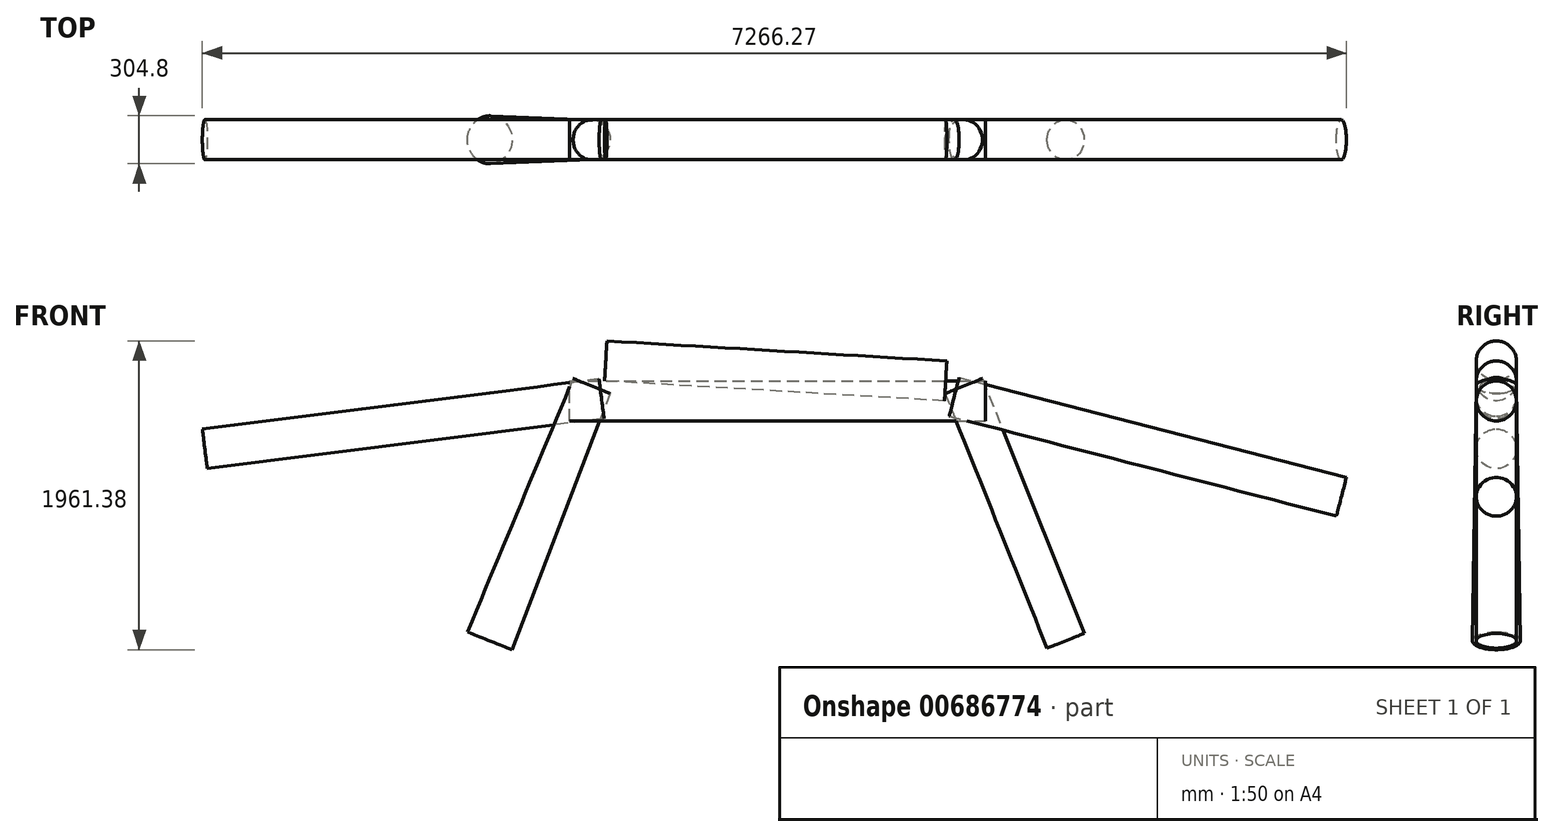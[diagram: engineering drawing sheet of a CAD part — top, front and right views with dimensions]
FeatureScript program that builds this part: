
annotation { "Feature Type Name" : "Feature", "Feature Type Description" : "" }
export const myFeature = defineFeature(function(context is Context, id is Id, definition is map)
    precondition{}
    {
        {
            var Q0;
            Q0=qCreatedBy(makeId("Front.planeOp"),FACE);
            var sketch = newSketch(context, id + "F0", { "sketchPlane" : qUnion([Q0])});
            skLineSegment(sketch, "E0", {"start": v(-1320.8, 0) * mm, "end": v(-1219.2, 0) * mm, "construction": true});
            skLineSegment(sketch, "E1", {"start": v(-1219.2, 0) * mm, "end": v(1219.2, 0) * mm, "construction": true});
            skLineSegment(sketch, "E2", {"start": v(1219.2, 0) * mm, "end": v(1320.8, 0) * mm, "construction": true});
            skLineSegment(sketch, "E3", {"start": v(-1181.47, 94.33) * mm, "end": v(-1219.2, 0) * mm, "construction": true});
            skLineSegment(sketch, "E4", {"start": v(-1219.2, 0) * mm, "end": v(-1828.8, -1524) * mm, "construction": true});
            skLineSegment(sketch, "E5", {"start": v(1181.47, 94.33) * mm, "end": v(1219.2, 0) * mm, "construction": true});
            skLineSegment(sketch, "E6", {"start": v(1219.2, 0) * mm, "end": v(1828.8, -1524) * mm, "construction": true});
            skLineSegment(sketch, "E7", {"start": v(1120.83, 25.4) * mm, "end": v(1219.2, 0) * mm, "construction": true});
            skLineSegment(sketch, "E8", {"start": v(1219.2, 0) * mm, "end": v(3580.17, -609.6) * mm, "construction": true});
            skLineSegment(sketch, "E9", {"start": v(-1118.4, 12.7) * mm, "end": v(-1219.2, 0) * mm, "construction": true});
            skLineSegment(sketch, "E10", {"start": v(-1219.2, 0) * mm, "end": v(-3638.47, -304.8) * mm, "construction": true});
            skLineSegment(sketch, "E11", {"start": v(1066.8, 127) * mm, "end": v(-1092.2, 254) * mm, "construction": true});
            skSolve(sketch);
        }
        {
            var Q0;
            Q0=sQuery(id+"F0.wireOp",EDGE,"E10");
            var Q1;
            Q1=sQuery(id+"F0.wireOp",VERTEX,"E10.end");
            cPlane(context, id + "F1", {"entities" : qUnion([Q0, Q1]), "cplaneType" : CPlaneType.LINE_POINT, "offset" : 25.4 * mm, "width" : 152.4 * mm, "height" : 152.4 * mm});
        }
        {
            var Q0;
            Q0=sQuery(id+"F0.wireOp",VERTEX,"E9.start");
            var Q1;
            Q1=sQuery(id+"F0.wireOp",EDGE,"E9");
            cPlane(context, id + "F2", {"entities" : qUnion([Q0, Q1]), "cplaneType" : CPlaneType.LINE_POINT, "offset" : 25.4 * mm, "width" : 152.4 * mm, "height" : 152.4 * mm});
        }
        {
            var Q0;
            Q0=qCreatedBy(id+"F1.planeOp",FACE);
            var sketch = newSketch(context, id + "F3", { "sketchPlane" : qUnion([Q0])});
            skCircle(sketch, "E12", {"center": v(0, 152.4) * mm, "radius": 127 * mm});
            skSolve(sketch);
        }
        {
            var Q0;
            Q0=qCreatedBy(id+"F2.planeOp",FACE);
            var sketch = newSketch(context, id + "F4", { "sketchPlane" : qUnion([Q0])});
            skCircle(sketch, "E13", {"center": v(0, 152.4) * mm, "radius": 127 * mm});
            skSolve(sketch);
        }
        {
            var Q0;
            Q0=makeQuery(id+"F3.imprint","IMPRINT",FACE,{"disambiguationData":[TD([[makeQuery(id+"F3.imprint","IMPRINT",EDGE,{"derivedFrom":sQuery(id+"F3.wireOp",EDGE,"E12")}),1.0]])]});
            var Q1;
            Q1=makeQuery(id+"F4.imprint","IMPRINT",FACE,{"disambiguationData":[TD([[makeQuery(id+"F4.imprint","IMPRINT",EDGE,{"derivedFrom":sQuery(id+"F4.wireOp",EDGE,"E13")}),1.0]])]});
            loft(context, id + "F5", {"sheetProfilesArray" : [{ "sheetProfileEntities" : qUnion([Q0]) }, { "sheetProfileEntities" : qUnion([Q1]) }]});
        }
        {
            var Q0;
            Q0=sQuery(id+"F0.wireOp",EDGE,"E4");
            var Q1;
            Q1=sQuery(id+"F0.wireOp",VERTEX,"E4.end");
            cPlane(context, id + "F6", {"entities" : qUnion([Q0, Q1]), "cplaneType" : CPlaneType.LINE_POINT, "offset" : 25.4 * mm, "width" : 152.4 * mm, "height" : 152.4 * mm});
        }
        {
            var Q0;
            Q0=sQuery(id+"F0.wireOp",VERTEX,"E3.start");
            var Q1;
            Q1=sQuery(id+"F0.wireOp",EDGE,"E3");
            cPlane(context, id + "F7", {"entities" : qUnion([Q0, Q1]), "cplaneType" : CPlaneType.LINE_POINT, "offset" : 25.4 * mm, "width" : 152.4 * mm, "height" : 152.4 * mm});
        }
        {
            var Q0;
            Q0=qCreatedBy(id+"F6.planeOp",FACE);
            var sketch = newSketch(context, id + "F8", { "sketchPlane" : qUnion([Q0])});
            skCircle(sketch, "E14", {"center": v(-1132, 0) * mm, "radius": 152.4 * mm});
            skSolve(sketch);
        }
        {
            var Q0;
            Q0=qCreatedBy(id+"F7.planeOp",FACE);
            var sketch = newSketch(context, id + "F9", { "sketchPlane" : qUnion([Q0])});
            skCircle(sketch, "E15", {"center": v(-1132, 0) * mm, "radius": 127 * mm});
            skSolve(sketch);
        }
        {
            var Q0;
            Q0=makeQuery(id+"F8.imprint","IMPRINT",FACE,{"disambiguationData":[TD([[makeQuery(id+"F8.imprint","IMPRINT",EDGE,{"derivedFrom":sQuery(id+"F8.wireOp",EDGE,"E14")}),1.0]])]});
            var Q1;
            Q1=makeQuery(id+"F9.imprint","IMPRINT",FACE,{"disambiguationData":[TD([[makeQuery(id+"F9.imprint","IMPRINT",EDGE,{"derivedFrom":sQuery(id+"F9.wireOp",EDGE,"E15")}),1.0]])]});
            loft(context, id + "F10", {"sheetProfilesArray" : [{ "sheetProfileEntities" : qUnion([Q0]) }, { "sheetProfileEntities" : qUnion([Q1]) }]});
        }
        {
            var Q0;
            Q0=sQuery(id+"F0.wireOp",EDGE,"E0");
            var Q1;
            Q1=sQuery(id+"F0.wireOp",VERTEX,"E0.start");
            cPlane(context, id + "F11", {"entities" : qUnion([Q0, Q1]), "cplaneType" : CPlaneType.LINE_POINT, "offset" : 25.4 * mm, "width" : 152.4 * mm, "height" : 152.4 * mm});
        }
        {
            var Q0;
            Q0=sQuery(id+"F0.wireOp",EDGE,"E2");
            var Q1;
            Q1=sQuery(id+"F0.wireOp",VERTEX,"E2.end");
            cPlane(context, id + "F12", {"entities" : qUnion([Q0, Q1]), "cplaneType" : CPlaneType.LINE_POINT, "offset" : 25.4 * mm, "width" : 152.4 * mm, "height" : 152.4 * mm});
        }
        {
            var Q0;
            Q0=qCreatedBy(id+"F12.planeOp",FACE);
            var sketch = newSketch(context, id + "F13", { "sketchPlane" : qUnion([Q0])});
            skCircle(sketch, "E16", {"center": v(0, 0) * mm, "radius": 127 * mm});
            skSolve(sketch);
        }
        {
            var Q0;
            Q0=qCreatedBy(id+"F11.planeOp",FACE);
            var sketch = newSketch(context, id + "F14", { "sketchPlane" : qUnion([Q0])});
            skCircle(sketch, "E17", {"center": v(0, 0) * mm, "radius": 127 * mm});
            skSolve(sketch);
        }
        {
            var Q0;
            Q0=makeQuery(id+"F14.imprint","IMPRINT",FACE,{"disambiguationData":[TD([[makeQuery(id+"F14.imprint","IMPRINT",EDGE,{"derivedFrom":sQuery(id+"F14.wireOp",EDGE,"E17")}),1.0]])]});
            var Q1;
            Q1=makeQuery(id+"F13.imprint","IMPRINT",FACE,{"disambiguationData":[TD([[makeQuery(id+"F13.imprint","IMPRINT",EDGE,{"derivedFrom":sQuery(id+"F13.wireOp",EDGE,"E16")}),1.0]])]});
            loft(context, id + "F15", {"sheetProfilesArray" : [{ "sheetProfileEntities" : qUnion([Q0]) }, { "sheetProfileEntities" : qUnion([Q1]) }]});
        }
        {
            var Q0;
            Q0=sQuery(id+"F0.wireOp",VERTEX,"E8.end");
            var Q1;
            Q1=sQuery(id+"F0.wireOp",EDGE,"E8");
            cPlane(context, id + "F16", {"entities" : qUnion([Q0, Q1]), "cplaneType" : CPlaneType.LINE_POINT, "offset" : 25.4 * mm, "width" : 152.4 * mm, "height" : 152.4 * mm});
        }
        {
            var Q0;
            Q0=sQuery(id+"F0.wireOp",EDGE,"E7");
            var Q1;
            Q1=sQuery(id+"F0.wireOp",VERTEX,"E7.start");
            cPlane(context, id + "F17", {"entities" : qUnion([Q0, Q1]), "cplaneType" : CPlaneType.LINE_POINT, "offset" : 25.4 * mm, "width" : 152.4 * mm, "height" : 152.4 * mm});
        }
        {
            var Q0;
            Q0=qCreatedBy(id+"F16.planeOp",FACE);
            var sketch = newSketch(context, id + "F18", { "sketchPlane" : qUnion([Q0])});
            skCircle(sketch, "E18", {"center": v(0, 304.8) * mm, "radius": 127 * mm});
            skSolve(sketch);
        }
        {
            var Q0;
            Q0=qCreatedBy(id+"F17.planeOp",FACE);
            var sketch = newSketch(context, id + "F19", { "sketchPlane" : qUnion([Q0])});
            skCircle(sketch, "E19", {"center": v(0, 304.8) * mm, "radius": 127 * mm});
            skSolve(sketch);
        }
        {
            var Q0;
            Q0=makeQuery(id+"F18.imprint","IMPRINT",FACE,{"disambiguationData":[TD([[makeQuery(id+"F18.imprint","IMPRINT",EDGE,{"derivedFrom":sQuery(id+"F18.wireOp",EDGE,"E18")}),1.0]])]});
            var Q1;
            Q1=makeQuery(id+"F19.imprint","IMPRINT",FACE,{"disambiguationData":[TD([[makeQuery(id+"F19.imprint","IMPRINT",EDGE,{"derivedFrom":sQuery(id+"F19.wireOp",EDGE,"E19")}),1.0]])]});
            loft(context, id + "F20", {"sheetProfilesArray" : [{ "sheetProfileEntities" : qUnion([Q0]) }, { "sheetProfileEntities" : qUnion([Q1]) }]});
        }
        {
            var Q0;
            Q0=sQuery(id+"F0.wireOp",EDGE,"E6");
            var Q1;
            Q1=sQuery(id+"F0.wireOp",VERTEX,"E6.end");
            cPlane(context, id + "F21", {"entities" : qUnion([Q0, Q1]), "cplaneType" : CPlaneType.LINE_POINT, "offset" : 25.4 * mm, "width" : 152.4 * mm, "height" : 152.4 * mm});
        }
        {
            var Q0;
            Q0=sQuery(id+"F0.wireOp",EDGE,"E5");
            var Q1;
            Q1=sQuery(id+"F0.wireOp",VERTEX,"E5.start");
            cPlane(context, id + "F22", {"entities" : qUnion([Q0, Q1]), "cplaneType" : CPlaneType.LINE_POINT, "offset" : 25.4 * mm, "width" : 152.4 * mm, "height" : 152.4 * mm});
        }
        {
            var Q0;
            Q0=qCreatedBy(id+"F22.planeOp",FACE);
            var sketch = newSketch(context, id + "F23", { "sketchPlane" : qUnion([Q0])});
            skCircle(sketch, "E20", {"center": v(1132, 0) * mm, "radius": 127 * mm});
            skSolve(sketch);
        }
        {
            var Q0;
            Q0=qCreatedBy(id+"F21.planeOp",FACE);
            var sketch = newSketch(context, id + "F24", { "sketchPlane" : qUnion([Q0])});
            skCircle(sketch, "E21", {"center": v(1132, 0) * mm, "radius": 127 * mm});
            skSolve(sketch);
        }
        {
            var Q0;
            Q0=makeQuery(id+"F24.imprint","IMPRINT",FACE,{"disambiguationData":[TD([[makeQuery(id+"F24.imprint","IMPRINT",EDGE,{"derivedFrom":sQuery(id+"F24.wireOp",EDGE,"E21")}),1.0]])]});
            var Q1;
            Q1=makeQuery(id+"F23.imprint","IMPRINT",FACE,{"disambiguationData":[TD([[makeQuery(id+"F23.imprint","IMPRINT",EDGE,{"derivedFrom":sQuery(id+"F23.wireOp",EDGE,"E20")}),1.0]])]});
            loft(context, id + "F25", {"sheetProfilesArray" : [{ "sheetProfileEntities" : qUnion([Q0]) }, { "sheetProfileEntities" : qUnion([Q1]) }]});
        }
        {
            var Q0;
            Q0=sQuery(id+"F0.wireOp",EDGE,"E11");
            var Q1;
            Q1=sQuery(id+"F0.wireOp",VERTEX,"E11.end");
            cPlane(context, id + "F26", {"entities" : qUnion([Q0, Q1]), "cplaneType" : CPlaneType.LINE_POINT, "offset" : 25.4 * mm, "width" : 152.4 * mm, "height" : 152.4 * mm});
        }
        {
            var Q0;
            Q0=sQuery(id+"F0.wireOp",EDGE,"E11");
            var Q1;
            Q1=sQuery(id+"F0.wireOp",VERTEX,"E11.start");
            cPlane(context, id + "F27", {"entities" : qUnion([Q0, Q1]), "cplaneType" : CPlaneType.LINE_POINT, "offset" : 25.4 * mm, "width" : 152.4 * mm, "height" : 152.4 * mm});
        }
        {
            var Q0;
            Q0=qCreatedBy(id+"F26.planeOp",FACE);
            var sketch = newSketch(context, id + "F28", { "sketchPlane" : qUnion([Q0])});
            skCircle(sketch, "E22", {"center": v(0, 189.43) * mm, "radius": 127 * mm});
            skSolve(sketch);
        }
        {
            var Q0;
            Q0=qCreatedBy(id+"F27.planeOp",FACE);
            var sketch = newSketch(context, id + "F29", { "sketchPlane" : qUnion([Q0])});
            skCircle(sketch, "E23", {"center": v(0, 189.43) * mm, "radius": 127 * mm});
            skSolve(sketch);
        }
        {
            var Q0;
            Q0=makeQuery(id+"F28.imprint","IMPRINT",FACE,{"disambiguationData":[TD([[makeQuery(id+"F28.imprint","IMPRINT",EDGE,{"derivedFrom":sQuery(id+"F28.wireOp",EDGE,"E22")}),1.0]])]});
            var Q1;
            Q1=makeQuery(id+"F29.imprint","IMPRINT",FACE,{"disambiguationData":[TD([[makeQuery(id+"F29.imprint","IMPRINT",EDGE,{"derivedFrom":sQuery(id+"F29.wireOp",EDGE,"E23")}),1.0]])]});
            loft(context, id + "F30", {"sheetProfilesArray" : [{ "sheetProfileEntities" : qUnion([Q0]) }, { "sheetProfileEntities" : qUnion([Q1]) }]});
        }
    });
